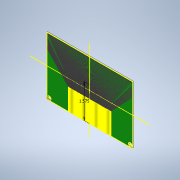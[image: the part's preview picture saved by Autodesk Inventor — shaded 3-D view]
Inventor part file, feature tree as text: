
AUTODESK INVENTOR PART (.ipt)
format: ipt  version: 2021 (Build 250183000, 183)  size: 4,113,920 bytes
history: native  units: in
note: dims shown in document units (in); Inventor stores cm internally (conversion verified against a paired STEP export)
features: sketch x12, extrude x9, projected_geometry x8, pattern_linear x7, mirror x5, hole x1
ambient origin geometry x8: Origin, YZ Plane, XZ Plane, XY Plane, X Axis, Y Axis, Z Axis, Center Point
bodies: Solid1 (feature_tree)
feature tree (42):
  extrude  "Extrusion1"  Depth=2.7in
  hole  "Hole1"  [1 undecoded]
  mirror  "Mirror3"
  sketch  "Sketch9"  dims[d42=0.1in d43=0.11in]
  extrude  "Extrusion5"  Depth=0.11in
  pattern_linear  "Rectangular Pattern6"  Count1=101 Spacing1=0.039in
  extrude  "Extrusion6"  Depth=0.0014in TaperAngle=0.0deg
  pattern_linear  "Rectangular Pattern7"  Count1=101 Spacing1=0.039in
  extrude  "Extrusion7"  TaperAngle=0.0deg  [1 undecoded]
  mirror  "Mirror4"
  extrude  "Extrusion9"  Depth=0.0014in
  pattern_linear  "Rectangular Pattern9"  Spacing1=0.25in  [1 undecoded]
  sketch  "Sketch16"  dims[d54=1.75in]
  pattern_linear  "Rectangular Pattern10"  Spacing1=0.008in  [1 undecoded]
  extrude  "Extrusion10"  Depth=1.0in
  pattern_linear  "Rectangular Pattern11"  Spacing1=0.0014in  [1 undecoded]
  mirror  "Mirror5"
  extrude  "Extrusion11"  Depth=0.016in
  mirror  "Mirror6"
  extrude  "Extrusion12"  Depth=0.0014in
  pattern_linear  "Rectangular Pattern12"  Spacing1=0.0198in  [1 undecoded]
  extrude  "Extrusion13"  Depth=0.0014in
  pattern_linear  "Rectangular Pattern13"  Spacing1=0.175in  [1 undecoded]
  mirror  "Mirror7"
  sketch  "Sketch1"  dims[d0=4.0in d1=2.7in]
  sketch  "Sketch7"  dims[d2=0.04in d3=0.0in d41=0.1719in]
  projected_geometry  "Projected Loop6"
  projected_geometry  "Projected Loop8"
  sketch  "Sketch11"  dims[d44=0.17in d45=0.75in d46=0.313in d47=0.164in d48=0.5635in d49=0.12in]
  projected_geometry  "Projected Loop9"
  sketch  "Sketch12"  dims[d50=0.8108in]
  sketch  "Sketch13"  dims[d52=1.5748in]
  sketch  "Sketch15"  dims[d53=0.02in]
  projected_geometry  "Projected Loop11"
  projected_geometry  "Projected Loop12"
  sketch  "Sketch17"  dims[d55=0.0in d56=0.0in d57=39.7638in d59=0.039in]
  projected_geometry  "Projected Loop13"
  sketch  "Sketch18"  dims[d60=0.032in d61=0.0014in d62=0.0in d63=39.7638in d65=0.039in]
  projected_geometry  "Projected Loop14"
  sketch  "Sketch19"  dims[d66=0.0197in d69=0.0in d70=0.0in]
  projected_geometry  "Projected Loop15"
  sketch  "Sketch20"  dims[d71=2.65in d82=2.0in d83=0.25in d84=0.008in d86=1.0in d87=0.0014in d88=0.0in d89=49.2126in d91=0.016in d92=39.7638in d94=0.039in d95=0.0198in d96=0.05in d97=0.175in d98=0.0in d99=0.0in d100=5.1181in d102=0.039in d103=0.008in d104=0.008in d105=0.008in d106=0.008in d107=0.008in d108=0.008in d109=0.008in d110=0.008in d111=0.008in d112=0.008in d113=0.008in d114=0.008in d115=0.008in d116=0.008in d117=0.008in d118=0.008in d119=0.008in d120=0.008in d121=0.008in d122=0.008in d123=0.008in d124=0.008in d125=0.008in d126=0.008in d127=0.008in d128=0.008in d129=0.008in d130=0.008in d131=0.008in d132=0.008in d133=0.008in d134=0.008in d135=0.008in d136=0.008in d137=0.008in d138=0.008in d139=0.008in d140=0.008in d141=0.008in d142=0.008in d143=0.008in d144=0.008in d145=0.008in d146=0.008in d147=0.008in d148=0.008in d149=0.008in d150=0.008in d151=0.008in d152=0.008in d153=0.008in d154=0.008in d155=0.008in d156=0.008in d157=0.008in d158=0.008in d159=0.008in d160=0.008in d161=0.008in d162=0.008in d163=0.008in d164=0.008in d165=0.008in d166=0.0014in d167=0.0in d168=0.008in d169=0.03in d170=0.0014in d171=0.0in d172=5.1181in d174=0.039in d175=0.032in d176=0.0014in d177=0.0in d178=39.7638in d180=0.039in]
note: 7 required parameter values undecoded (feature->parameter linkage not recoverable at this tier; creation-order binding heuristic only, values carry confidence <= 0.55)
